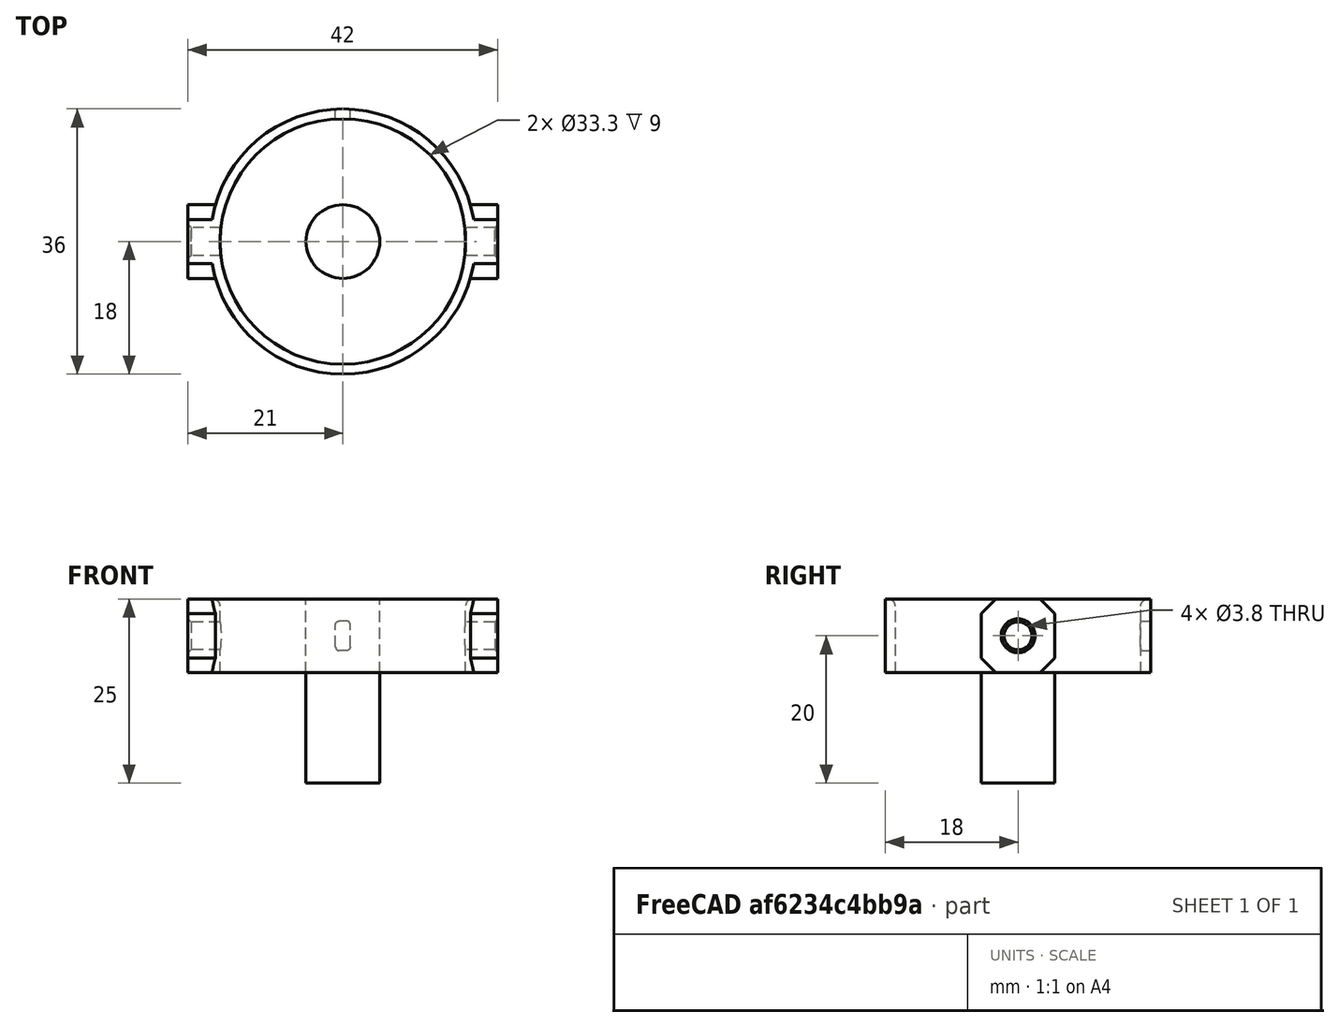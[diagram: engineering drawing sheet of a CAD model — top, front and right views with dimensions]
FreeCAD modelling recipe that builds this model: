
FCSTD DOCUMENT  (FreeCAD 0.19R24291 (Git))
Label: drone-brushed-fan-mount
License: Other
LicenseURL: GPL3
objects: Part::Cylinder×4, Part::Cut×4, Part::Box×3, Part::Fillet×2, Part::MultiFuse×2, Part::Chamfer×2, Part::Feature×1
note: 18 computed .brp shape members not serialized (recipe doc carries the construction recipe); baked Part::Feature solids carry a one-line shape summary decoded from their .brp

FEATURE [Part::Cylinder] Cylinder
  Angle = 360
  AttacherType = Attacher::AttachEngine3D
  Height = 10
  Radius = 16.65
FEATURE [Part::Cylinder] Cylinder001
  Angle = 360
  AttacherType = Attacher::AttachEngine3D
  Height = 10
  Radius = 18
FEATURE [Part::Cut] Cut
  Base = -> Cylinder001
  Tool = -> Cylinder
FEATURE [Part::Fillet] Fillet
  Base = -> Cut
  Edges = 1 edges r=1: [Edge4]
FEATURE [Part::Box] Box  label="Cube"
  AttacherType = Attacher::AttachEngine3D
  Height = 10
  Length = 5
  Placement = pos=(16,-5,0) rot=(0,0,1;0rad)
  Width = 10
FEATURE [Part::Box] Box001  label="Cube001"
  AttacherType = Attacher::AttachEngine3D
  Height = 10
  Length = 5
  Placement = pos=(-21,-5,0) rot=(0,0,1;0rad)
  Width = 10
FEATURE [Part::Cylinder] Cylinder002
  Angle = 360
  AttacherType = Attacher::AttachEngine3D
  Height = 10
  Radius = 17.65
FEATURE [Part::MultiFuse] Fusion
  Shapes = -> [Box001,Box]
FEATURE [Part::Chamfer] Chamfer
  Base = -> Fusion
  Edges = 8 edges r=2: [Edge9,Edge10,Edge11,Edge12,Edge21,Edge22,Edge23,Edge24]
FEATURE [Part::Cut] Cut001
  Base = -> Chamfer
  Tool = -> Cylinder002
FEATURE [Part::MultiFuse] Fusion001
  Shapes = -> [Fillet,Cut001]
FEATURE [Part::Cylinder] Cylinder003
  Angle = 360
  AttacherType = Attacher::AttachEngine3D
  Height = 51
  Placement = pos=(25,0,5) rot=(0,1,0;4.71239rad)
  Radius = 1.9
FEATURE [Part::Cut] Cut002
  Base = -> Fusion001
  Tool = -> Cylinder003
FEATURE [Part::Chamfer] Chamfer001
  Base = -> Cut002
  Edges = 2 edges r=0.4: [Edge41,Edge61]
FEATURE [Part::Feature] Fusion002001
  shape: bbox 42 x 38.21 x 25 mm, 36 faces, 2 solids (baked)
FEATURE [Part::Box] Box002  label="Cube002"
  AttacherType = Attacher::AttachEngine3D
  Height = 4
  Length = 2
  Placement = pos=(-1,15,3) rot=(0,0,1;0rad)
  Width = 6
FEATURE [Part::Fillet] Fillet001
  Base = -> Box002
  Edges = 4 edges r=0.5: [Edge2,Edge4,Edge6,Edge8]
FEATURE [Part::Cut] Cut003
  Base = -> Chamfer001
  Tool = -> Fillet001
